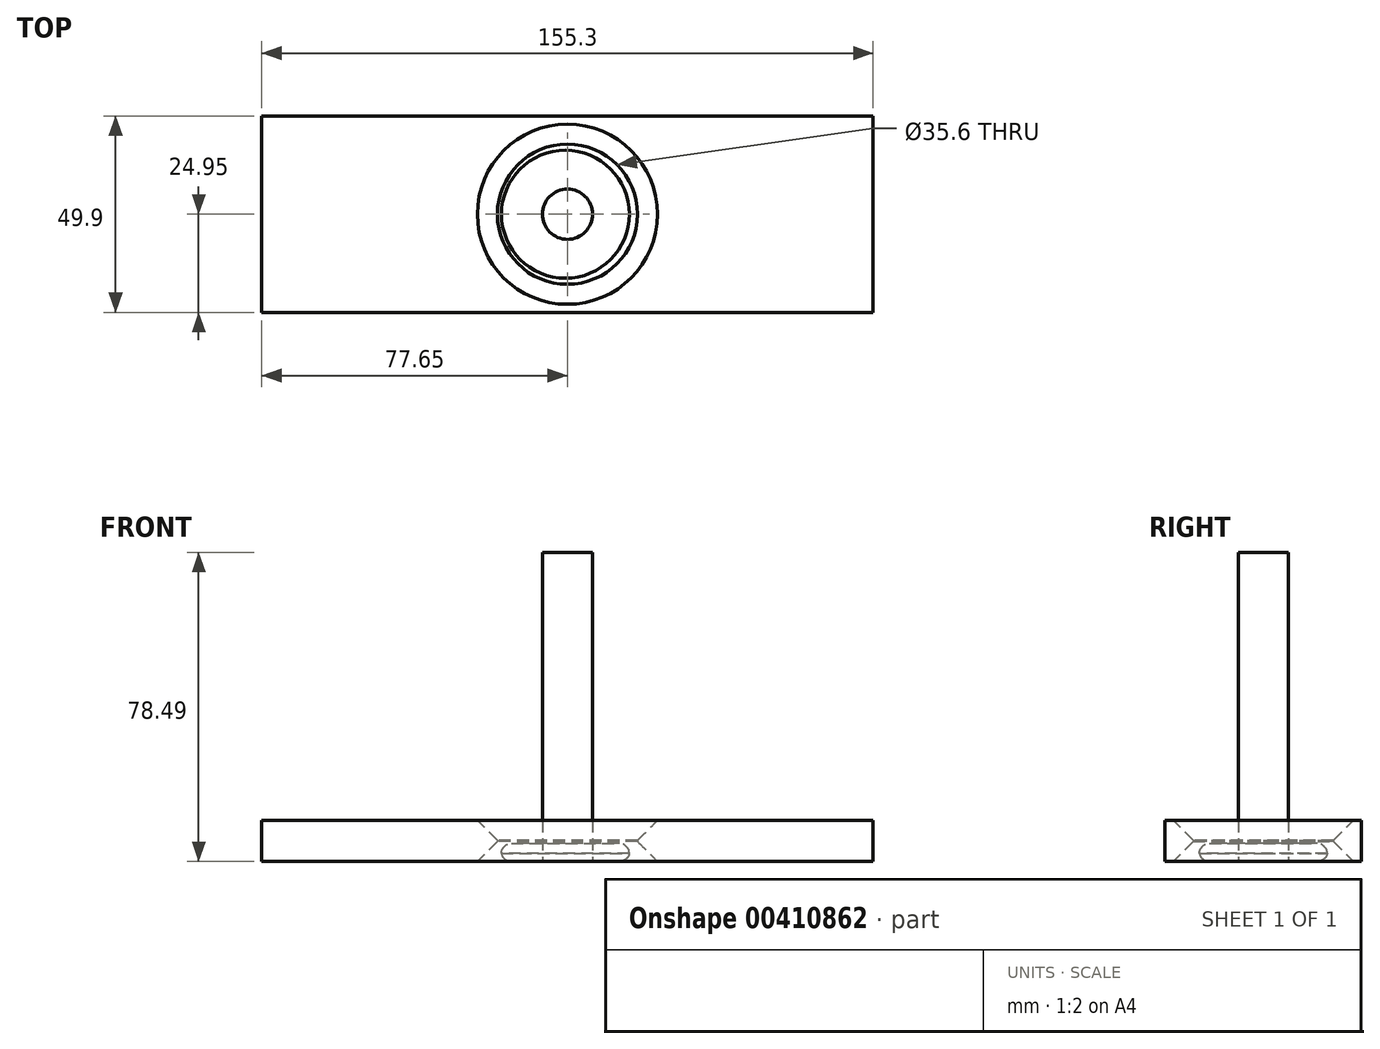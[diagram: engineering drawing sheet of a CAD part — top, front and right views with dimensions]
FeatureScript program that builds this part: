
annotation { "Feature Type Name" : "Feature", "Feature Type Description" : "" }
export const myFeature = defineFeature(function(context is Context, id is Id, definition is map)
    precondition{}
    {
        {
            var Q0;
            Q0=qCreatedBy(makeId("Top.planeOp"),FACE);
            var sketch = newSketch(context, id + "F0", { "sketchPlane" : qUnion([Q0])});
            skLineSegment(sketch, "E0.bottom", {"start": v(77.65, -24.95) * mm, "end": v(-77.65, -24.95) * mm});
            skLineSegment(sketch, "E0.top", {"start": v(77.65, 24.95) * mm, "end": v(-77.65, 24.95) * mm});
            skLineSegment(sketch, "E0.left", {"start": v(77.65, -24.95) * mm, "end": v(77.65, 24.95) * mm});
            skLineSegment(sketch, "E0.right", {"start": v(-77.65, -24.95) * mm, "end": v(-77.65, 24.95) * mm});
            skPoint(sketch, "E0.middle", {"position": v(0, 0) * mm});
            skCircle(sketch, "E1", {"center": v(0, 0) * mm, "radius": 17.8 * mm});
            skSolve(sketch);
        }
        {
            var Q0;
            Q0=makeQuery(id+"F0.imprint","IMPRINT",FACE,{"disambiguationData":[TD([[makeQuery(id+"F0.imprint","IMPRINT",EDGE,{"derivedFrom":sQuery(id+"F0.wireOp",EDGE,"E0.bottom")}),-1.0]])]});
            extrude(context, id + "F1", {"entities" : qUnion([Q0]), "depth" : 4.57 * mm});
        }
        {
            var Q0;
            Q0=makeQuery(id+"F1.opExtrude","CAP_FACE",FACE,{"disambiguationData":[OSD([sQuery(id+"F0.wireOp",EDGE,"E0.bottom"),sQuery(id+"F0.wireOp",EDGE,"E0.top"),sQuery(id+"F0.wireOp",EDGE,"E0.left"),sQuery(id+"F0.wireOp",EDGE,"E0.right"),sQuery(id+"F0.wireOp",EDGE,"Mq9GsJAD-XjAf-LoLl-6A1C-Hlng52lcd7Be"),sQuery(id+"F0.wireOp",EDGE,"E1"),sQuery(id+"F0.wireOp",EDGE,"L4oHv1zY-29Rk-QTJX-WhaE-I1HkD6L7DtBP")])],"isStart":false});
            var sketch = newSketch(context, id + "F2", { "sketchPlane" : qUnion([Q0])});
            skLineSegment(sketch, "E2.bottom", {"start": v(77.65, -24.95) * mm, "end": v(-77.65, -24.95) * mm});
            skLineSegment(sketch, "E2.top", {"start": v(77.65, 24.95) * mm, "end": v(-77.65, 24.95) * mm});
            skLineSegment(sketch, "E2.left", {"start": v(77.65, -24.95) * mm, "end": v(77.65, 24.95) * mm});
            skLineSegment(sketch, "E2.right", {"start": v(-77.65, -24.95) * mm, "end": v(-77.65, 24.95) * mm});
            skPoint(sketch, "E2.middle", {"position": v(0, 0) * mm});
            skCircle(sketch, "E3", {"center": v(0, 0) * mm, "radius": 17.8 * mm});
            skSolve(sketch);
        }
        {
            var Q0;
            Q0 = qSketchRegion(id + "F2", true);
            extrude(context, id + "F3", {"entities" : qUnion([Q0]), "operationType" : NewBodyOperationType.ADD, "depth" : 5.84 * mm});
        }
        {
            var Q0;
            Q0=qCreatedBy(makeId("Top.planeOp"),FACE);
            var sketch = newSketch(context, id + "F4", { "sketchPlane" : qUnion([Q0])});
            skCircle(sketch, "E4", {"center": v(-0.52, 0) * mm, "radius": 16.25 * mm});
            skSolve(sketch);
        }
        {
            var Q0;
            Q0 = qSketchRegion(id + "F4", true);
            extrude(context, id + "F5", {"entities" : qUnion([Q0]), "depth" : 4.57 * mm});
        }
        {
            var Q0;
            Q0=makeQuery(id+"F5.opExtrude","CAP_EDGE",EDGE,{"disambiguationData":[OSD([sQuery(id+"F4.wireOp",EDGE,"E4")])],"isStart":false});
            fillet(context, id + "F6", {"entities" : qUnion([Q0]), "radius" : 2.54 * mm, "tangentPropagation" : true, "allowEdgeOverflow" : false});
        }
        {
            var Q0;
            Q0=makeQuery(id+"F5.opExtrude","CAP_EDGE",EDGE,{"disambiguationData":[OSD([sQuery(id+"F4.wireOp",EDGE,"E4")])],"isStart":true});
            fillet(context, id + "F7", {"entities" : qUnion([Q0]), "radius" : 2.54 * mm, "tangentPropagation" : true, "allowEdgeOverflow" : false});
        }
        {
            var Q0;
            Q0=qCreatedBy(makeId("Top.planeOp"),FACE);
            var sketch = newSketch(context, id + "F8", { "sketchPlane" : qUnion([Q0])});
            skCircle(sketch, "E5", {"center": v(0, 0) * mm, "radius": 6.38 * mm});
            skSolve(sketch);
        }
        {
            var Q0;
            Q0 = qSketchRegion(id + "F8", true);
            extrude(context, id + "F9", {"entities" : qUnion([Q0]), "depth" : 78.49 * mm});
        }
        {
            var Q0;
            Q0=makeQuery(id+"F1.opExtrude","CAP_EDGE",EDGE,{"disambiguationData":[OSD([sQuery(id+"F0.wireOp",EDGE,"E1")])],"isStart":true});
            chamfer(context, id + "F10", {"entities" : qUnion([Q0]), "width" : 5.08 * mm, "tangentPropagation" : true});
        }
        {
            var Q0;
            Q0=makeQuery(id+"F3.opExtrude","CAP_EDGE",EDGE,{"disambiguationData":[OSD([sQuery(id+"F2.wireOp",EDGE,"E3")])],"isStart":false});
            chamfer(context, id + "F11", {"entities" : qUnion([Q0]), "width" : 5.08 * mm, "tangentPropagation" : true});
        }
    });
